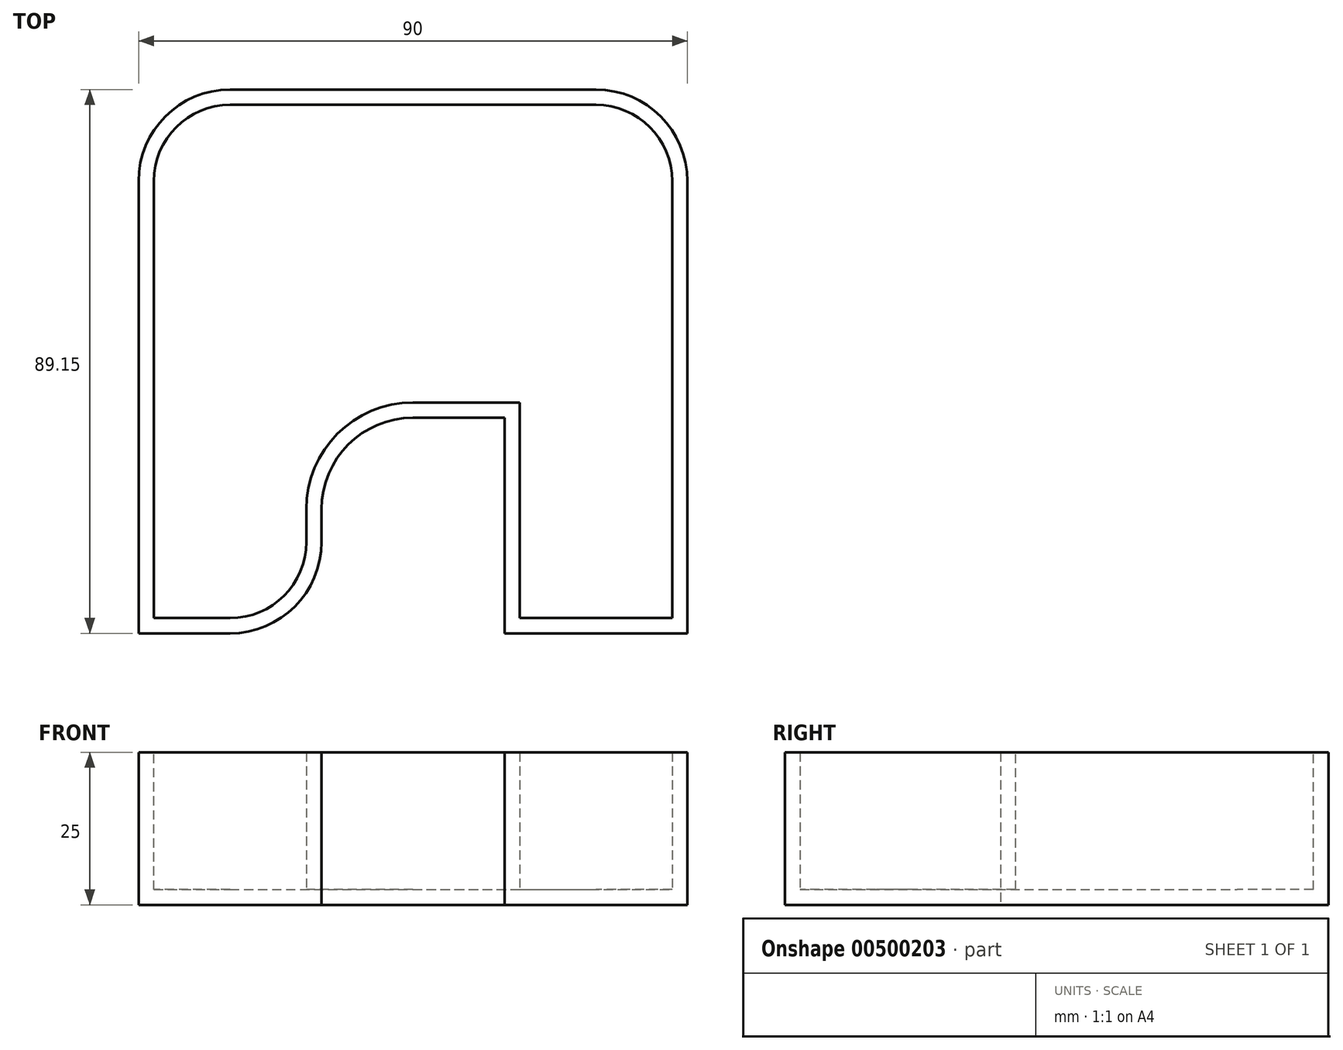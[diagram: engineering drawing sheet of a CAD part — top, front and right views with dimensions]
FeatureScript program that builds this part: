
annotation { "Feature Type Name" : "Feature", "Feature Type Description" : "" }
export const myFeature = defineFeature(function(context is Context, id is Id, definition is map)
    precondition{}
    {
        {
            var Q0;
            Q0=qCreatedBy(makeId("Top.planeOp"),FACE);
            var sketch = newSketch(context, id + "F0", { "sketchPlane" : qUnion([Q0])});
            skLineSegment(sketch, "E0.bottom", {"start": v(0, 0) * mm, "end": v(15, 0) * mm});
            skLineSegment(sketch, "E0.top", {"start": v(15, 89.15) * mm, "end": v(75, 89.15) * mm});
            skLineSegment(sketch, "E0.left", {"start": v(0, 0) * mm, "end": v(0, 74.15) * mm});
            skLineSegment(sketch, "E0.right", {"start": v(90, 0) * mm, "end": v(90, 74.15) * mm});
            skLineSegment(sketch, "E1", {"start": v(45, 35.36) * mm, "end": v(60, 35.36) * mm});
            skLineSegment(sketch, "E2", {"start": v(30, 20.36) * mm, "end": v(30, 15) * mm});
            skLineSegment(sketch, "E3", {"start": v(60, 35.36) * mm, "end": v(60, 0) * mm});
            skLineSegment(sketch, "E4.trimOffspring", {"start": v(60, 0) * mm, "end": v(90, 0) * mm});
            skPoint(sketch, "E5.visualSharp", {"position": v(0, 89.15) * mm});
            skArc(sketch, "E5.filletArc", {"start": v(15, 89.15) * mm, "mid": v(4.4, 84.76) * mm, "end": v(0, 74.15) * mm});
            skPoint(sketch, "E6.visualSharp", {"position": v(90, 89.15) * mm});
            skArc(sketch, "E6.filletArc", {"start": v(90, 74.15) * mm, "mid": v(85.6, 84.76) * mm, "end": v(75, 89.15) * mm});
            skPoint(sketch, "E7.visualSharp", {"position": v(30, 0) * mm});
            skArc(sketch, "E7.filletArc", {"start": v(15, 0) * mm, "mid": v(25.6, 4.4) * mm, "end": v(30, 15) * mm});
            skPoint(sketch, "E8.visualSharp", {"position": v(30, 35.36) * mm});
            skArc(sketch, "E8.filletArc", {"start": v(45, 35.36) * mm, "mid": v(34.4, 30.96) * mm, "end": v(30, 20.36) * mm});
            skSolve(sketch);
        }
        {
            var Q0;
            Q0 = qSketchRegion(id + "F0", true);
            extrude(context, id + "F1", {"entities" : qUnion([Q0]), "depth" : 25 * mm});
        }
        {
            var Q0;
            Q0=makeQuery(id+"F1.opExtrude","CAP_FACE",FACE,{"disambiguationData":[OSD([sQuery(id+"F0.wireOp",EDGE,"E0.bottom"),sQuery(id+"F0.wireOp",EDGE,"E0.top"),sQuery(id+"F0.wireOp",EDGE,"E0.left"),sQuery(id+"F0.wireOp",EDGE,"E0.right"),sQuery(id+"F0.wireOp",EDGE,"E1"),sQuery(id+"F0.wireOp",EDGE,"E2"),sQuery(id+"F0.wireOp",EDGE,"E3"),sQuery(id+"F0.wireOp",EDGE,"E4.trimOffspring"),sQuery(id+"F0.wireOp",EDGE,"E5.filletArc"),sQuery(id+"F0.wireOp",EDGE,"E6.filletArc"),sQuery(id+"F0.wireOp",EDGE,"E7.filletArc"),sQuery(id+"F0.wireOp",EDGE,"E8.filletArc")])],"isStart":false});
            shell(context, id + "F2", {"entities" : qUnion([Q0]), "thickness" : 2.5 * mm});
        }
    });
